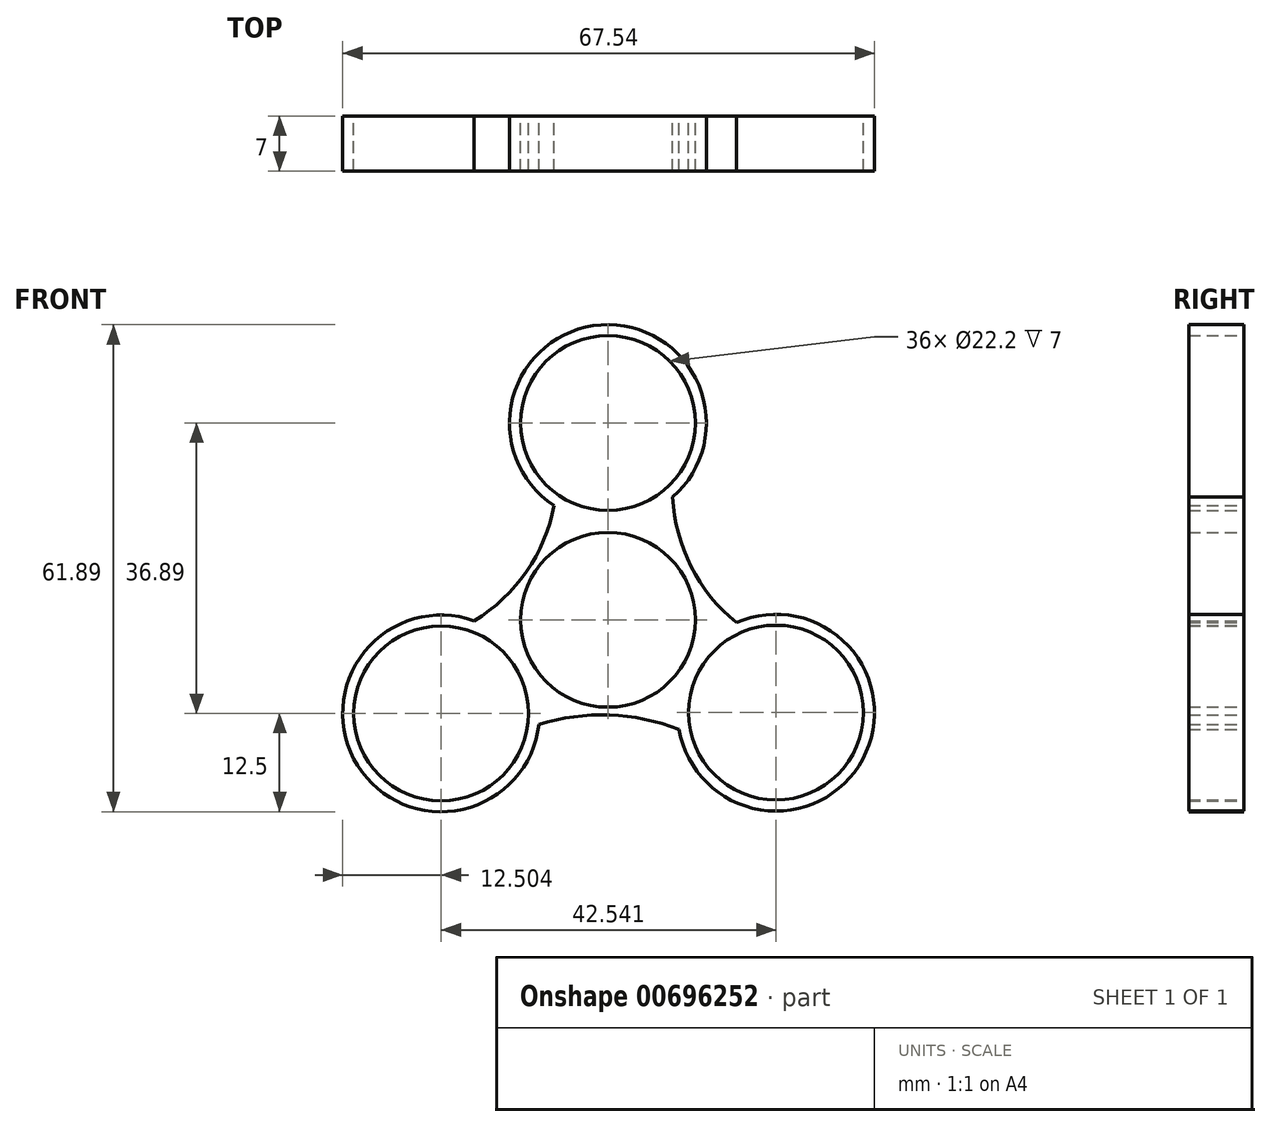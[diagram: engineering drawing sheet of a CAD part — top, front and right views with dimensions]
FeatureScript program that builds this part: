
annotation { "Feature Type Name" : "Feature", "Feature Type Description" : "" }
export const myFeature = defineFeature(function(context is Context, id is Id, definition is map)
    precondition{}
    {
        {
            var Q0;
            Q0=qCreatedBy(makeId("Front.planeOp"),FACE);
            var sketch = newSketch(context, id + "F0", { "sketchPlane" : qUnion([Q0])});
            skCircle(sketch, "E0", {"center": v(0, 0) * mm, "radius": 11.1 * mm});
            skCircle(sketch, "E1", {"center": v(0, 25) * mm, "radius": 11.1 * mm});
            skCircle(sketch, "E2.1.0", {"center": v(-21.19, -11.9) * mm, "radius": 11.1 * mm});
            skCircle(sketch, "E2.2.0", {"center": v(21.35, -11.8) * mm, "radius": 11.1 * mm});
            skPoint(sketch, "E2.center", {"position": v(0.06, 0.44) * mm});
            skCircle(sketch, "E3", {"center": v(0, 25) * mm, "radius": 12.5 * mm});
            skArc(sketch, "E4", {"start": v(-18.71, -1.07) * mm, "mid": v(-10.94, 5.33) * mm, "end": v(-6.83, 14.53) * mm});
            skArc(sketch, "E5", {"start": v(10.62, -14.6) * mm, "mid": v(0.26, -12.1) * mm, "end": v(-10.25, -13.81) * mm});
            skArc(sketch, "E6", {"start": v(8.22, 15.58) * mm, "mid": v(10.96, 6.03) * mm, "end": v(17.62, -1.34) * mm});
            skCircle(sketch, "E7", {"center": v(-21.19, -11.9) * mm, "radius": 12.5 * mm});
            skCircle(sketch, "E8", {"center": v(21.35, -11.8) * mm, "radius": 12.5 * mm});
            skSolve(sketch);
        }
        {
            var Q0;
            Q0 = qSketchRegion(id + "F0", true);
            extrude(context, id + "F1", {"entities" : qUnion([Q0]), "depth" : 7 * mm, "offsetDistance" : 25 * mm});
        }
    });
